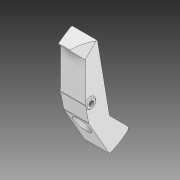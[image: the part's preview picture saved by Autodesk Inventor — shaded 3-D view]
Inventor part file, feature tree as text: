
AUTODESK INVENTOR PART (.ipt)
format: ipt  version: 2020 (Build 240168000, 168)  size: 229,888 bytes
history: native  units: in
note: dims shown in document units (in); Inventor stores cm internally (conversion verified against a paired STEP export)
features: extrude x6, sketch x6, chamfer x2, projected_geometry x1, imported_body x1
ambient origin geometry x8: Origin, YZ Plane, XZ Plane, XY Plane, X Axis, Y Axis, Z Axis, Center Point
bodies: Solid1 (feature_tree)
feature tree (16):
  extrude  "Extrusion1"  Depth=0.1969in
  extrude  "Extrusion2"  Depth=0.1575in
  extrude  "Extrusion3"  Depth=0.0197in TaperAngle=45.0deg
  chamfer  "Chamfer1"  Distance=0.0197in
  extrude  "Extrusion4"  Depth=0.1496in
  chamfer  "Chamfer2"  [1 undecoded]
  extrude  "Extrusion5"  Depth=0.1181in TaperAngle=0.0deg
  extrude  "Extrusion6"  [1 undecoded]
  sketch  "Sketch1"  dims[d0=0.4528in d1=0.0in d2=0.1969in]
  projected_geometry  "Projected Loop1"
  sketch  "Sketch2"  dims[d3=0.4528in d4=0.0in d5=0.1575in]
  sketch  "Sketch3"  dims[d6=0.0197in d7=0.0in d8=0.0197in d9=0.0787in d10=45.0deg]
  sketch  "Sketch4"  dims[d11=0.1575in d12=0.0197in d13=0.0in]
  sketch  "Sketch5"  dims[d14=0.0197in d15=0.0787in d16=45.0deg d17=0.1496in]
  sketch  "Sketch6"  dims[d18=0.5512in d19=0.0in d20=0.0in d21=0.1181in d22=0.0in]
  imported_body  "Base1"
note: 2 required parameter values undecoded (feature->parameter linkage not recoverable at this tier; creation-order binding heuristic only, values carry confidence <= 0.55)
